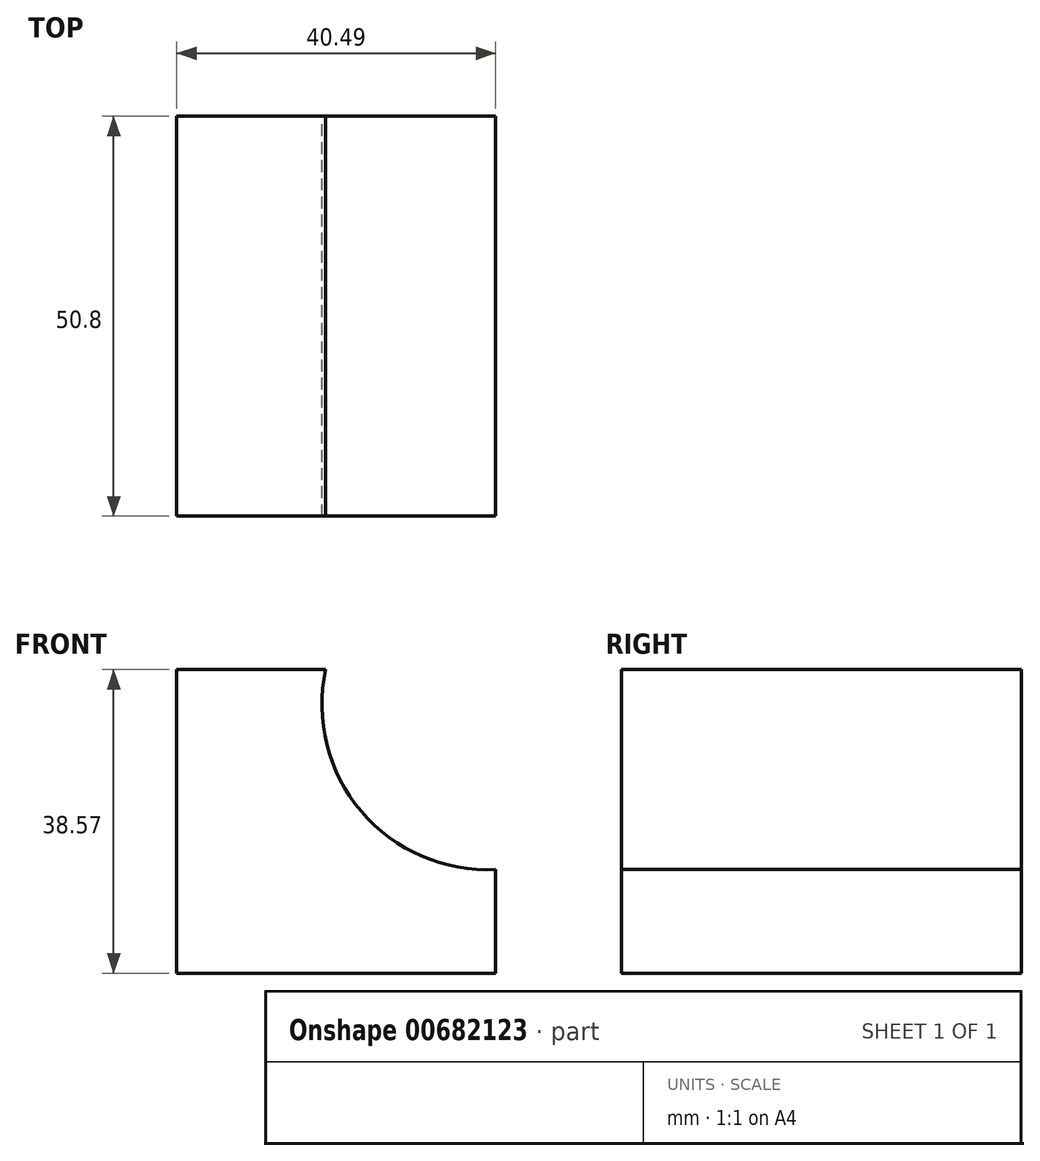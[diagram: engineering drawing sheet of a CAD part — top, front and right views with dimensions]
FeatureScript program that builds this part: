
annotation { "Feature Type Name" : "Feature", "Feature Type Description" : "" }
export const myFeature = defineFeature(function(context is Context, id is Id, definition is map)
    precondition{}
    {
        {
            var Q0;
            Q0=qCreatedBy(makeId("Front.planeOp"),FACE);
            var sketch = newSketch(context, id + "F0", { "sketchPlane" : qUnion([Q0])});
            skArc(sketch, "E0", {"start": v(-29.5, 47.26) * mm, "mid": v(-24.97, 29.24) * mm, "end": v(-7.92, 21.86) * mm});
            skLineSegment(sketch, "E1", {"start": v(-7.92, 21.86) * mm, "end": v(-7.92, 8.69) * mm});
            skLineSegment(sketch, "E2", {"start": v(-7.92, 8.69) * mm, "end": v(-48.4, 8.69) * mm});
            skLineSegment(sketch, "E3", {"start": v(-48.4, 8.69) * mm, "end": v(-48.4, 47.26) * mm});
            skLineSegment(sketch, "E4", {"start": v(-48.4, 47.26) * mm, "end": v(-29.5, 47.26) * mm});
            skSolve(sketch);
        }
        {
            var Q0;
            Q0 = qSketchRegion(id + "F0", true);
            extrude(context, id + "F1", {"entities" : qUnion([Q0]), "depth" : 50.8 * mm, "offsetDistance" : 25.4 * mm});
        }
    });
